FCSTD DOCUMENT  (FreeCAD 0.16R5861 (Git))
Label: 12mm_double_bearing_holder_v0.7
License: All rights reserved
LicenseURL: http://en.wikipedia.org/wiki/All_rights_reserved
objects: Sketcher::SketchObject×17, PartDesign::Pocket×9, PartDesign::Pad×8, PartDesign::Chamfer×5, PartDesign::Fillet×3, Part::Feature×3, PartDesign::LinearPattern×2
note: 64 computed .brp shape members not serialized (recipe doc carries the construction recipe); baked Part::Feature solids carry a one-line shape summary decoded from their .brp

FEATURE [Sketcher::SketchObject] Sketch
  sketch-geometry (8):
    g0: Circle CenterX=0 CenterY=12 CenterZ=0 NormalX=0 NormalY=0 NormalZ=1 Radius=11.4
    g1: LineSegment StartX=0 StartY=0 StartZ=0 EndX=22 EndY=0 EndZ=0
    g2: LineSegment StartX=0 StartY=0 StartZ=0 EndX=-22 EndY=0 EndZ=0
    g3: LineSegment StartX=-22 StartY=0 StartZ=0 EndX=-22 EndY=7 EndZ=0
    g4: LineSegment StartX=-22 StartY=7 StartZ=0 EndX=-14.1421 EndY=7 EndZ=0
    g5: LineSegment StartX=22 StartY=0 StartZ=0 EndX=22 EndY=7 EndZ=0
    g6: LineSegment StartX=22 StartY=7 StartZ=0 EndX=14.1421 EndY=7 EndZ=0
    g7: ArcOfCircle CenterX=0 CenterY=12 CenterZ=0 NormalX=0 NormalY=0 NormalZ=1 Radius=15 StartAngle=5.94335 EndAngle=9.76461
  constraints (24):
    c: PointOnObject(g0,g-2)
    c: Radius(g0) = 11.4
    c: DistanceY(g-1,g0) = 12
    c: Coincident(g-1,g1)
    c: PointOnObject(g1,g-1)
    c: Coincident(g-1,g2)
    c: PointOnObject(g2,g-1)
    c: Equal(g2,g1)
    c: DistanceX(g2,g1) = 44
    c: Coincident(g2,g3)
    c: Vertical(g3)
    c: Coincident(g3,g4)
    c: Horizontal(g4)
    c: Coincident(g1,g5)
    c: Vertical(g5)
    c: Coincident(g5,g6)
    c: Horizontal(g6)
    c: Equal(g6,g4)
    c: Equal(g3,g5)
    c: DistanceY(g3) = 7
    c: Coincident(g7,g0)
    c: Coincident(g7,g4)
    c: Coincident(g7,g6)
    c: Radius(g7) = 15
FEATURE [PartDesign::Pad] Pad
  Length = 100
  Length2 = 100
  Sketch = -> Sketch
  Type = 0
FEATURE [PartDesign::Fillet] Fillet
  Base = -> Pad [Edge8,Edge11]
  Radius = 6
FEATURE [Sketcher::SketchObject] Sketch001
  ExternalGeometry = -> [Fillet]
  Placement = pos=(0,0,0) rot=(1,0,0;1.5708rad)
  Support = -> Fillet [Face9]
  sketch-geometry (8):
    g0: LineSegment [constr] StartX=-16 StartY=4.5 StartZ=0 EndX=16 EndY=4.5 EndZ=0
    g1: LineSegment [constr] StartX=16 StartY=4.5 StartZ=0 EndX=16 EndY=95.5 EndZ=0
    g2: LineSegment [constr] StartX=16 StartY=95.5 StartZ=0 EndX=-16 EndY=95.5 EndZ=0
    g3: LineSegment [constr] StartX=-16 StartY=95.5 StartZ=0 EndX=-16 EndY=4.5 EndZ=0
    g4: Circle CenterX=-16 CenterY=95.5 CenterZ=0 NormalX=0 NormalY=0 NormalZ=1 Radius=3.5
    g5: Circle CenterX=-16 CenterY=4.5 CenterZ=0 NormalX=0 NormalY=0 NormalZ=1 Radius=3.5
    g6: Circle CenterX=16 CenterY=4.5 CenterZ=0 NormalX=0 NormalY=0 NormalZ=1 Radius=3.5
    g7: Circle CenterX=16 CenterY=95.5 CenterZ=0 NormalX=0 NormalY=0 NormalZ=1 Radius=3.5
  constraints (20):
    c: Coincident(g0,g1)
    c: Coincident(g1,g2)
    c: Coincident(g2,g3)
    c: Coincident(g3,g0)
    c: Horizontal(g0)
    c: Horizontal(g2)
    c: Vertical(g1)
    c: Vertical(g3)
    c: DistanceX(g2) = -32
    c: DistanceY(g1) = 91
    c: DistanceX(g2,g-3) = -6
    c: DistanceY(g2,g-3) = 4.5
    c: Coincident(g4,g2)
    c: Coincident(g5,g0)
    c: Coincident(g6,g0)
    c: Coincident(g7,g1)
    c: Equal(g7,g4)
    c: Equal(g4,g5)
    c: Equal(g5,g6)
    c: Radius(g7) = 3.5
FEATURE [PartDesign::Pocket] Pocket
  Length = 5
  Sketch = -> Sketch001
  Type = 1
FEATURE [Sketcher::SketchObject] Sketch002
  ExternalGeometry = -> [Pocket]
  Placement = pos=(0,0,0) rot=(1,0,0;1.5708rad)
  Support = -> Pocket [Face9]
  sketch-geometry (8):
    g0: Circle CenterX=-16 CenterY=95.5 CenterZ=0 NormalX=0 NormalY=0 NormalZ=1 Radius=2
    g1: Circle CenterX=-16 CenterY=95.5 CenterZ=0 NormalX=0 NormalY=0 NormalZ=1 Radius=4
    g2: Circle CenterX=16 CenterY=95.5 CenterZ=0 NormalX=0 NormalY=0 NormalZ=1 Radius=4
    g3: Circle CenterX=16 CenterY=95.5 CenterZ=0 NormalX=0 NormalY=0 NormalZ=1 Radius=2
    g4: Circle CenterX=16 CenterY=4.5 CenterZ=0 NormalX=0 NormalY=0 NormalZ=1 Radius=4
    g5: Circle CenterX=16 CenterY=4.5 CenterZ=0 NormalX=0 NormalY=0 NormalZ=1 Radius=2
    g6: Circle CenterX=-16 CenterY=4.5 CenterZ=0 NormalX=0 NormalY=0 NormalZ=1 Radius=4
    g7: Circle CenterX=-16 CenterY=4.5 CenterZ=0 NormalX=0 NormalY=0 NormalZ=1 Radius=2
  constraints (16):
    c: Coincident(g0,g-3)
    c: Coincident(g1,g0)
    c: Coincident(g2,g-4)
    c: Coincident(g3,g2)
    c: Coincident(g4,g-6)
    c: Coincident(g5,g4)
    c: Coincident(g6,g-5)
    c: Coincident(g7,g6)
    c: Equal(g6,g4)
    c: Equal(g4,g2)
    c: Equal(g2,g1)
    c: Equal(g5,g7)
    c: Equal(g7,g0)
    c: Equal(g0,g3)
    c: Radius(g3) = 2
    c: Radius(g2) = 4
FEATURE [PartDesign::Pad] Pad001
  Length = 7
  Length2 = 100
  Reversed = true
  Sketch = -> Sketch002
  Type = 0
FEATURE [Sketcher::SketchObject] Sketch003
  ExternalGeometry = -> [Pad001]
  Placement = pos=(0,0,0) rot=(1,0,0;1.5708rad)
  Support = -> Pad001 [Face7]
  sketch-geometry (8):
    g0: LineSegment StartX=-22 StartY=94 StartZ=0 EndX=-15 EndY=84.003 EndZ=0
    g1: LineSegment StartX=-15 StartY=84.003 StartZ=0 EndX=-15 EndY=15.997 EndZ=0
    g2: LineSegment StartX=-15 StartY=15.997 StartZ=0 EndX=-22 EndY=6 EndZ=0
    g3: LineSegment StartX=22 StartY=94 StartZ=0 EndX=15 EndY=84.003 EndZ=0
    g4: LineSegment StartX=15 StartY=84.003 StartZ=0 EndX=15 EndY=15.997 EndZ=0
    g5: LineSegment StartX=15 StartY=15.997 StartZ=0 EndX=22 EndY=6 EndZ=0
    g6: LineSegment StartX=22 StartY=6 StartZ=0 EndX=22 EndY=94 EndZ=0
    g7: LineSegment StartX=-22 StartY=6 StartZ=0 EndX=-22 EndY=94 EndZ=0
  constraints (24):
    c: PointOnObject(g0,g-3)
    c: Coincident(g0,g1)
    c: Vertical(g1)
    c: Coincident(g1,g2)
    c: PointOnObject(g2,g-3)
    c: PointOnObject(g3,g-4)
    c: Coincident(g3,g4)
    c: Vertical(g4)
    c: Coincident(g4,g5)
    c: PointOnObject(g5,g-4)
    c: Coincident(g5,g6)
    c: Coincident(g6,g3)
    c: Coincident(g7,g2)
    c: Coincident(g7,g0)
    c: Equal(g0,g2)
    c: Equal(g2,g5)
    c: Equal(g5,g3)
    c: Equal(g1,g4)
    c: DistanceX(g0,g-3) = -7
    c: DistanceX(g3,g-4) = 7
    c: DistanceY(g2,g-3) = -6
    c: DistanceY(g3,g-4) = 6
    c: DistanceY(g5,g-4) = -6
    c: Angle(g5,g4) = 2.53073
FEATURE [PartDesign::Pocket] Pocket001
  Length = 5
  Sketch = -> Sketch003
  Type = 1
FEATURE [PartDesign::Chamfer] Chamfer
  Base = -> Pocket001 [Edge30,Edge71]
  Size = 8
FEATURE [Sketcher::SketchObject] Sketch004
  ExternalGeometry = -> [Chamfer]
  Placement = pos=(0,0,100) rot=(0,0,1;0rad)
  Support = -> Chamfer [Face10]
  sketch-geometry (2):
    g0: Circle CenterX=0 CenterY=12 CenterZ=0 NormalX=0 NormalY=0 NormalZ=1 Radius=11.8
    g1: Circle CenterX=0 CenterY=12 CenterZ=0 NormalX=0 NormalY=0 NormalZ=1 Radius=11.2
  constraints (6):
    c: Coincident(g0,g-3)
    c: Coincident(g1,g0)
    c: Radius(g0) = 11.8
    c: Radius(g-3) = 11.4
    c: Radius(g-3) = 11.4
    c: Radius(g1) = 11.2
FEATURE [PartDesign::Pad] Pad002
  Length = 100
  Length2 = 100
  Reversed = true
  Sketch = -> Sketch004
  Type = 0
FEATURE [Sketcher::SketchObject] Sketch005
  Placement = pos=(0,0,0) rot=(1,0,0;3.14159rad)
  Support = -> Pad002 [Face7]
  sketch-geometry (3):
    g0: ArcOfCircle CenterX=0 CenterY=-13.5 CenterZ=0 NormalX=0 NormalY=0 NormalZ=1 Radius=15 StartAngle=1.11977 EndAngle=2.02182
    g1: LineSegment [constr] StartX=0 StartY=0 StartZ=0 EndX=0 EndY=1.5 EndZ=0
    g2: LineSegment StartX=-6.53835 StartY=0 StartZ=0 EndX=6.53835 EndY=0 EndZ=0
  constraints (10):
    c: PointOnObject(g0,g-2)
    c: PointOnObject(g0,g-1)
    c: PointOnObject(g0,g-1)
    c: Coincident(g1,g-1)
    c: PointOnObject(g1,g0)
    c: Vertical(g1)
    c: DistanceY(g1) = 1.5
    c: Radius(g0) = 15
    c: Coincident(g2,g0)
    c: Coincident(g2,g0)
FEATURE [PartDesign::Pad] Pad003
  Length = 100
  Length2 = 100
  Reversed = true
  Sketch = -> Sketch005
  Type = 0
FEATURE [Part::Feature] Pad003001  label="Pad004"
  shape: bbox 44 x 28.5 x 100 mm, 37 faces (baked)
FEATURE [Sketcher::SketchObject] Sketch006
  ExternalGeometry = -> [Pad003001]
  Placement = pos=(0,0,0) rot=(1,0,0;1.5708rad)
  Support = -> Pad003001 [Face36]
  sketch-geometry (8):
    g0: LineSegment StartX=-22 StartY=100 StartZ=0 EndX=-20 EndY=100 EndZ=0
    g1: LineSegment StartX=-20 StartY=100 StartZ=0 EndX=-20 EndY=0 EndZ=0
    g2: LineSegment StartX=-20 StartY=0 StartZ=0 EndX=-22 EndY=0 EndZ=0
    g3: LineSegment StartX=-22 StartY=0 StartZ=0 EndX=-22 EndY=100 EndZ=0
    g4: LineSegment StartX=22 StartY=100 StartZ=0 EndX=20 EndY=100 EndZ=0
    g5: LineSegment StartX=20 StartY=100 StartZ=0 EndX=20 EndY=0 EndZ=0
    g6: LineSegment StartX=20 StartY=0 StartZ=0 EndX=22 EndY=0 EndZ=0
    g7: LineSegment StartX=22 StartY=0 StartZ=0 EndX=22 EndY=100 EndZ=0
  constraints (22):
    c: Coincident(g0,g1)
    c: Coincident(g1,g2)
    c: Coincident(g2,g3)
    c: Coincident(g3,g0)
    c: Horizontal(g0)
    c: Horizontal(g2)
    c: Vertical(g1)
    c: Vertical(g3)
    c: Coincident(g0,g-4)
    c: PointOnObject(g1,g-1)
    c: Coincident(g4,g5)
    c: Coincident(g5,g6)
    c: Coincident(g6,g7)
    c: Coincident(g7,g4)
    c: Horizontal(g4)
    c: Horizontal(g6)
    c: Vertical(g5)
    c: Vertical(g7)
    c: Coincident(g4,g-3)
    c: PointOnObject(g5,g-1)
    c: Equal(g2,g6)
    c: DistanceX(g6) = 2
FEATURE [PartDesign::Pocket] Pocket002
  Length = 5
  Sketch = -> Sketch006
  Type = 1
FEATURE [Sketcher::SketchObject] Sketch007
  ExternalGeometry = -> [Pocket002]
  Placement = pos=(0,0,0) rot=(1,0,0;1.5708rad)
  Support = -> Pocket002 [Face15]
  sketch-geometry (4):
    g0: Circle CenterX=-16 CenterY=95.5 CenterZ=0 NormalX=0 NormalY=0 NormalZ=1 Radius=4
    g1: Circle CenterX=16 CenterY=95.5 CenterZ=0 NormalX=0 NormalY=0 NormalZ=1 Radius=4
    g2: Circle CenterX=-16 CenterY=4.5 CenterZ=0 NormalX=0 NormalY=0 NormalZ=1 Radius=4
    g3: Circle CenterX=16 CenterY=4.5 CenterZ=0 NormalX=0 NormalY=0 NormalZ=1 Radius=4
  constraints (8):
    c: Coincident(g0,g-5)
    c: Coincident(g1,g-6)
    c: Coincident(g2,g-3)
    c: Coincident(g3,g-4)
    c: Equal(g2,g3)
    c: Equal(g3,g0)
    c: Equal(g0,g1)
    c: Radius(g1) = 4
FEATURE [PartDesign::Pocket] Pocket003
  Length = 5
  Sketch = -> Sketch007
  Type = 1
FEATURE [Sketcher::SketchObject] Sketch008
  ExternalGeometry = -> [Pocket003]
  Placement = pos=(0,0,0) rot=(1,0,0;1.5708rad)
  Support = -> Pocket003 [Face19]
  sketch-geometry (8):
    g0: Circle CenterX=16 CenterY=4.5 CenterZ=0 NormalX=0 NormalY=0 NormalZ=1 Radius=4
    g1: Circle CenterX=-16 CenterY=4.5 CenterZ=0 NormalX=0 NormalY=0 NormalZ=1 Radius=4
    g2: Circle CenterX=-16 CenterY=95.5 CenterZ=0 NormalX=0 NormalY=0 NormalZ=1 Radius=4
    g3: Circle CenterX=16 CenterY=95.5 CenterZ=0 NormalX=0 NormalY=0 NormalZ=1 Radius=4
    g4: Circle CenterX=-16 CenterY=4.5 CenterZ=0 NormalX=0 NormalY=0 NormalZ=1 Radius=2
    g5: Circle CenterX=16 CenterY=4.5 CenterZ=0 NormalX=0 NormalY=0 NormalZ=1 Radius=2
    g6: Circle CenterX=-16 CenterY=95.5 CenterZ=0 NormalX=0 NormalY=0 NormalZ=1 Radius=2
    g7: Circle CenterX=16 CenterY=95.5 CenterZ=0 NormalX=0 NormalY=0 NormalZ=1 Radius=2
  constraints (16):
    c: Coincident(g0,g-6)
    c: Coincident(g1,g-5)
    c: Coincident(g2,g-3)
    c: Coincident(g3,g-4)
    c: Equal(g3,g2)
    c: Equal(g2,g1)
    c: Equal(g1,g0)
    c: Tangent(g-7,g0)
    c: Coincident(g4,g1)
    c: Coincident(g5,g0)
    c: Coincident(g6,g2)
    c: Coincident(g7,g3)
    c: Equal(g7,g6)
    c: Equal(g6,g4)
    c: Equal(g4,g5)
    c: Radius(g4) = 2
FEATURE [PartDesign::Pad] Pad003002
  Length = 7
  Length2 = 100
  Reversed = true
  Sketch = -> Sketch008
  Type = 0
FEATURE [Sketcher::SketchObject] Sketch009
  ExternalGeometry = -> [Pad003002]
  Placement = pos=(0,0,100) rot=(0,0,1;0rad)
  Support = -> Pad003002 [Face17]
  sketch-geometry (1):
    g0: Circle CenterX=0 CenterY=12 CenterZ=0 NormalX=0 NormalY=0 NormalZ=1 Radius=11.35
  constraints (2):
    c: Coincident(g0,g-3)
    c: Radius(g0) = 11.35
FEATURE [PartDesign::Pocket] Pocket004
  Length = 5
  Sketch = -> Sketch009
  Type = 1
FEATURE [PartDesign::Chamfer] Chamfer001
  Base = -> Pocket004 [Edge73,Edge29]
  Size = 0.5
FEATURE [Sketcher::SketchObject] Sketch010
  ExternalGeometry = -> [Chamfer001]
  Placement = pos=(0,0,100) rot=(0,0,1;0rad)
  Support = -> Chamfer001 [Face20]
  sketch-geometry (2):
    g0: Circle CenterX=0 CenterY=12 CenterZ=0 NormalX=0 NormalY=0 NormalZ=1 Radius=11.15
    g1: Circle CenterX=0 CenterY=12 CenterZ=0 NormalX=0 NormalY=0 NormalZ=1 Radius=13
  constraints (4):
    c: Coincident(g0,g-3)
    c: Coincident(g1,g0)
    c: Radius(g1) = 13
    c: Radius(g0) = 11.15
FEATURE [PartDesign::Pad] Pad003003
  Length = 100
  Length2 = 100
  Reversed = true
  Sketch = -> Sketch010
  Type = 0
FEATURE [Part::Feature] Pad003003001  label="Pad003004"
  shape: bbox 40 x 28.5 x 100 mm, 43 faces (baked)
FEATURE [PartDesign::Chamfer] Chamfer002
  Base = -> Pad003003001 [Edge106,Edge111]
  Size = 1
FEATURE [Sketcher::SketchObject] Sketch011
  ExternalGeometry = -> [Chamfer002]
  Placement = pos=(0,0,100) rot=(0,0,1;0rad)
  Support = -> Chamfer002 [Face1]
  sketch-geometry (1):
    g0: Circle CenterX=0 CenterY=12 CenterZ=0 NormalX=0 NormalY=0 NormalZ=1 Radius=11.3
  constraints (1):
    c: Radius(g0) = 11.3
FEATURE [PartDesign::Pocket] Pocket005
  Length = 5
  Sketch = -> Sketch011
  Type = 1
FEATURE [Sketcher::SketchObject] Sketch012
  ExternalGeometry = -> [Pocket005]
  Placement = pos=(0,0,100) rot=(0,0,1;0rad)
  Support = -> Pocket005 [Face1]
  sketch-geometry (2):
    g0: Circle CenterX=0 CenterY=12 CenterZ=0 NormalX=0 NormalY=0 NormalZ=1 Radius=13
    g1: Circle CenterX=0 CenterY=12 CenterZ=0 NormalX=0 NormalY=0 NormalZ=1 Radius=10.75
  constraints (4):
    c: Coincident(g0,g-3)
    c: Coincident(g1,g0)
    c: Radius(g0) = 13
    c: Radius(g1) = 10.75
FEATURE [PartDesign::Pad] Pad003003002
  Length = 1
  Length2 = 100
  Reversed = true
  Sketch = -> Sketch012
  Type = 0
FEATURE [PartDesign::LinearPattern] LinearPattern
  Direction = -> Pad003003002 [Edge8]
  Length = 5
  Occurrences = 2
  Originals = -> [Pad003003002]
  Reversed = true
FEATURE [PartDesign::Fillet] Fillet001
  Base = -> LinearPattern [Edge145,Edge142,Edge135,Edge141]
  Radius = 0.49
FEATURE [Sketcher::SketchObject] Sketch013
  ExternalGeometry = -> [Fillet001]
  Placement = pos=(0,0,0) rot=(1,0,0;3.14159rad)
  Support = -> Fillet001 [Face18]
  sketch-geometry (2):
    g0: Circle CenterX=0 CenterY=-12 CenterZ=0 NormalX=0 NormalY=0 NormalZ=1 Radius=12.25
    g1: Circle CenterX=0 CenterY=-12 CenterZ=0 NormalX=0 NormalY=0 NormalZ=1 Radius=10.75
  constraints (4):
    c: Coincident(g0,g-3)
    c: Coincident(g1,g0)
    c: Radius(g1) = 10.75
    c: Radius(g0) = 12.25
FEATURE [PartDesign::Pad] Pad003003003
  Length = 1
  Length2 = 100
  Reversed = true
  Sketch = -> Sketch013
  Type = 0
FEATURE [PartDesign::LinearPattern] LinearPattern001
  Direction = -> Pad003003003 [Edge39]
  Length = 5
  Occurrences = 2
  Originals = -> [Pad003003003]
FEATURE [PartDesign::Fillet] Fillet002
  Base = -> LinearPattern001 [Edge17,Edge59,Edge2,Edge3]
  Radius = 0.49
FEATURE [Part::Feature] Fillet002001  label="Fillet003"
  shape: bbox 40 x 28.5 x 100 mm, 63 faces (baked)
FEATURE [Sketcher::SketchObject] Sketch014
  ExternalGeometry = -> [Fillet002001]
  Placement = pos=(0,0,100) rot=(0,0,1;0rad)
  Support = -> Fillet002001 [Face61]
  sketch-geometry (1):
    g0: Circle CenterX=0 CenterY=12 CenterZ=0 NormalX=0 NormalY=0 NormalZ=1 Radius=11.24
  constraints (2):
    c: Coincident(g0,g-3)
    c: Equal(g-3,g0)
FEATURE [PartDesign::Pocket] Pocket006
  Length = 1
  Sketch = -> Sketch014
  Type = 0
FEATURE [Sketcher::SketchObject] Sketch015
  ExternalGeometry = -> [Pocket006]
  Placement = pos=(0,0,0) rot=(1,0,0;3.14159rad)
  Support = -> Pocket006 [Face5]
  sketch-geometry (1):
    g0: Circle CenterX=0 CenterY=-12 CenterZ=0 NormalX=0 NormalY=0 NormalZ=1 Radius=11.24
  constraints (2):
    c: Coincident(g0,g-3)
    c: Equal(g-3,g0)
FEATURE [PartDesign::Pocket] Pocket007
  Length = 1
  Sketch = -> Sketch015
  Type = 0
FEATURE [PartDesign::Chamfer] Chamfer003
  Base = -> Pocket007 [Edge84,Edge34]
  Size = 0.99
FEATURE [Sketcher::SketchObject] Sketch016
  ExternalGeometry = -> [Chamfer003]
  Placement = pos=(0,0,100) rot=(0,0,1;0rad)
  Support = -> Chamfer003 [Face21]
  sketch-geometry (1):
    g0: Circle CenterX=0 CenterY=12 CenterZ=0 NormalX=0 NormalY=0 NormalZ=1 Radius=11
  constraints (2):
    c: Coincident(g0,g-4)
    c: Radius(g0) = 11
FEATURE [PartDesign::Pocket] Pocket008
  Length = 5
  Sketch = -> Sketch016
  Type = 1
FEATURE [PartDesign::Chamfer] Chamfer004
  Base = -> Pocket008 [Edge141,Edge145,Edge133,Edge136]
  Size = 0.3
